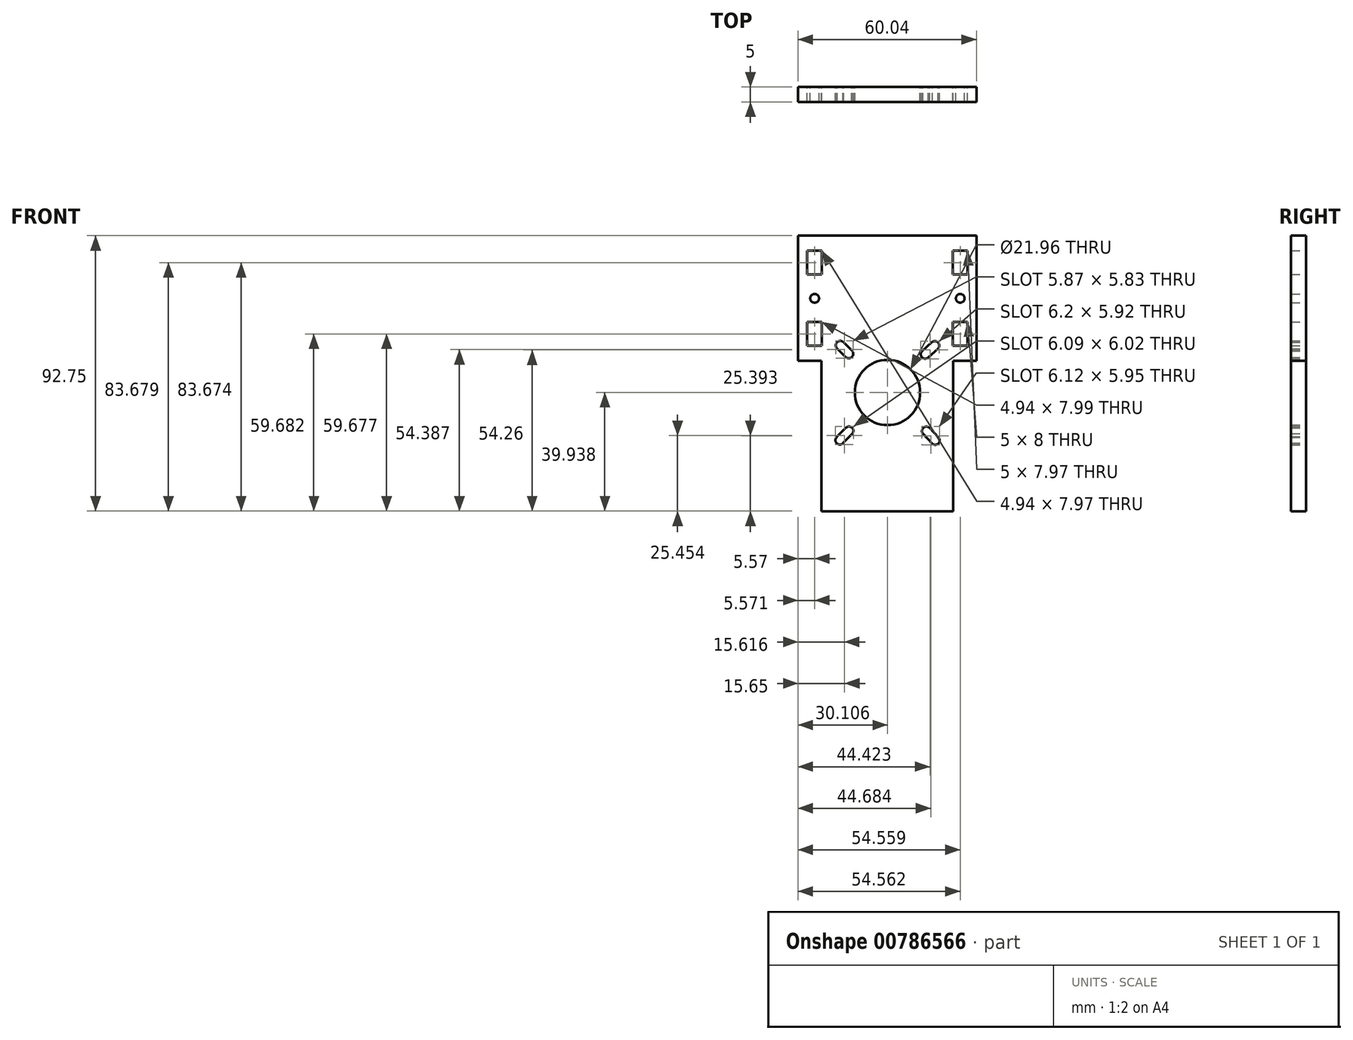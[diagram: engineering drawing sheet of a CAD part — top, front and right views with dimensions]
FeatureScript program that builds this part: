
annotation { "Feature Type Name" : "Feature", "Feature Type Description" : "" }
export const myFeature = defineFeature(function(context is Context, id is Id, definition is map)
    precondition{}
    {
        {
            var Q0;
            Q0=qCreatedBy(makeId("Front.planeOp"),FACE);
            var sketch = newSketch(context, id + "F0", { "sketchPlane" : qUnion([Q0])});
            skLineSegment(sketch, "E0.bottom", {"start": v(-30.76, 29.63) * mm, "end": v(29.28, 29.63) * mm});
            skLineSegment(sketch, "E0.top", {"start": v(-22.85, -63.12) * mm, "end": v(21.5, -63.12) * mm});
            skLineSegment(sketch, "E0.left", {"start": v(-30.76, 29.63) * mm, "end": v(-30.76, -12.55) * mm});
            skLineSegment(sketch, "E0.right", {"start": v(29.28, 29.63) * mm, "end": v(29.28, -12.55) * mm});
            skLineSegment(sketch, "E1.top", {"start": v(-30.76, -12.55) * mm, "end": v(-22.85, -12.55) * mm});
            skLineSegment(sketch, "E1.right", {"start": v(-22.85, -63.12) * mm, "end": v(-22.85, -12.55) * mm});
            skLineSegment(sketch, "E2.top", {"start": v(29.28, -12.55) * mm, "end": v(21.5, -12.55) * mm});
            skLineSegment(sketch, "E2.right", {"start": v(21.5, -63.12) * mm, "end": v(21.5, -12.55) * mm});
            skLineSegment(sketch, "E3.bottom", {"start": v(-27.66, 24.54) * mm, "end": v(-22.72, 24.54) * mm});
            skLineSegment(sketch, "E3.top", {"start": v(-27.66, 16.57) * mm, "end": v(-22.72, 16.57) * mm});
            skLineSegment(sketch, "E3.left", {"start": v(-27.66, 24.54) * mm, "end": v(-27.66, 16.57) * mm});
            skLineSegment(sketch, "E3.right", {"start": v(-22.72, 24.54) * mm, "end": v(-22.72, 16.57) * mm});
            skLineSegment(sketch, "E4.bottom", {"start": v(21.3, 24.55) * mm, "end": v(26.3, 24.55) * mm});
            skLineSegment(sketch, "E4.top", {"start": v(21.3, 16.57) * mm, "end": v(26.3, 16.57) * mm});
            skLineSegment(sketch, "E4.left", {"start": v(21.3, 24.55) * mm, "end": v(21.3, 16.57) * mm});
            skLineSegment(sketch, "E4.right", {"start": v(26.3, 24.55) * mm, "end": v(26.3, 16.57) * mm});
            skLineSegment(sketch, "E5.bottom", {"start": v(21.3, 0.56) * mm, "end": v(26.3, 0.56) * mm});
            skLineSegment(sketch, "E5.top", {"start": v(21.3, -7.44) * mm, "end": v(26.3, -7.44) * mm});
            skLineSegment(sketch, "E5.left", {"start": v(21.3, 0.56) * mm, "end": v(21.3, -7.44) * mm});
            skLineSegment(sketch, "E5.right", {"start": v(26.3, 0.56) * mm, "end": v(26.3, -7.44) * mm});
            skLineSegment(sketch, "E6.bottom", {"start": v(-27.66, 0.55) * mm, "end": v(-22.72, 0.55) * mm});
            skLineSegment(sketch, "E6.top", {"start": v(-27.66, -7.44) * mm, "end": v(-22.72, -7.44) * mm});
            skLineSegment(sketch, "E6.left", {"start": v(-27.66, 0.55) * mm, "end": v(-27.66, -7.44) * mm});
            skLineSegment(sketch, "E6.right", {"start": v(-22.72, 0.55) * mm, "end": v(-22.72, -7.44) * mm});
            skCircle(sketch, "E7", {"center": v(-25.17, 8.52) * mm, "radius": 1.48 * mm});
            skPoint(sketch, "E7.first.point", {"position": v(-25.2, 10) * mm});
            skPoint(sketch, "E7.second.point", {"position": v(-26.2, 7.46) * mm});
            skPoint(sketch, "E7.third.point", {"position": v(-23.83, 7.9) * mm});
            skCircle(sketch, "E8", {"center": v(23.84, 8.53) * mm, "radius": 1.47 * mm});
            skPoint(sketch, "E8.first.point", {"position": v(23.8, 10) * mm});
            skPoint(sketch, "E8.second.point", {"position": v(22.65, 7.66) * mm});
            skPoint(sketch, "E8.third.point", {"position": v(25.14, 7.85) * mm});
            skCircle(sketch, "E9", {"center": v(-0.65, -23.18) * mm, "radius": 10.98 * mm});
            skPoint(sketch, "E9.first.point", {"position": v(-10.51, -18.35) * mm});
            skPoint(sketch, "E9.second.point", {"position": v(9.28, -18.51) * mm});
            skPoint(sketch, "E9.third.point", {"position": v(-0.59, -34.16) * mm});
            skArc(sketch, "E10", {"start": v(-15.43, -6.33) * mm, "mid": v(-17.6, -6.24) * mm, "end": v(-17.56, -8.41) * mm});
            skArc(sketch, "E11", {"start": v(-14.72, -11.22) * mm, "mid": v(-12.53, -11.13) * mm, "end": v(-12.76, -8.95) * mm});
            skArc(sketch, "E12", {"start": v(16.35, -8.46) * mm, "mid": v(16.32, -6.35) * mm, "end": v(14.2, -6.3) * mm});
            skArc(sketch, "E13", {"start": v(11.06, -9.22) * mm, "mid": v(10.95, -11.34) * mm, "end": v(13.08, -11.4) * mm});
            skArc(sketch, "E14", {"start": v(-17.65, -38.1) * mm, "mid": v(-17.74, -40.25) * mm, "end": v(-15.59, -40.24) * mm});
            skArc(sketch, "E15", {"start": v(-12.54, -37.1) * mm, "mid": v(-12.57, -35.04) * mm, "end": v(-14.63, -35.05) * mm});
            skArc(sketch, "E16", {"start": v(14.48, -40.44) * mm, "mid": v(16.53, -40.3) * mm, "end": v(16.43, -38.23) * mm});
            skArc(sketch, "E17", {"start": v(13.55, -35.16) * mm, "mid": v(11.48, -35) * mm, "end": v(11.24, -37.07) * mm});
            skLineSegment(sketch, "E18", {"start": v(-15.43, -6.33) * mm, "end": v(-12.76, -8.95) * mm});
            skLineSegment(sketch, "E19", {"start": v(-17.56, -8.41) * mm, "end": v(-14.72, -11.22) * mm});
            skLineSegment(sketch, "E20", {"start": v(11.06, -9.22) * mm, "end": v(14.2, -6.3) * mm});
            skLineSegment(sketch, "E21", {"start": v(13.08, -11.4) * mm, "end": v(16.35, -8.46) * mm});
            skLineSegment(sketch, "E22", {"start": v(13.52, -35.12) * mm, "end": v(16.43, -38.23) * mm});
            skLineSegment(sketch, "E23", {"start": v(11.24, -37.07) * mm, "end": v(14.48, -40.44) * mm});
            skLineSegment(sketch, "E24", {"start": v(-17.65, -38.1) * mm, "end": v(-14.63, -35.05) * mm});
            skLineSegment(sketch, "E25", {"start": v(-15.59, -40.24) * mm, "end": v(-12.54, -37.1) * mm});
            skSolve(sketch);
        }
        {
            var Q0;
            Q0 = qSketchRegion(id + "F0", true);
            extrude(context, id + "F1", {"entities" : qUnion([Q0]), "depth" : 5 * mm, "offsetDistance" : 25.4 * mm});
        }
    });
